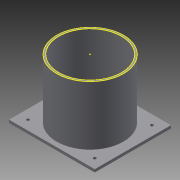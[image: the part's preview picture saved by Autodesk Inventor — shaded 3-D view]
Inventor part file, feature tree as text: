
AUTODESK INVENTOR PART (.ipt)
format: ipt  version: 2013 (Build 170138000, 138)  size: 115,200 bytes
history: native  units: mm
features: sketch x5, extrude x3, other x1, hole x1
ambient origin geometry x8: Origin, YZ Plane, XZ Plane, XY Plane, X Axis, Y Axis, Z Axis, Center Point
feature tree (10):
  other  "ソリッド1"
  extrude  "押し出し1"  Depth=70.0mm
  extrude  "押し出し2"  Depth=66.0mm
  extrude  "押し出し3"  Depth=90.0mm
  sketch  "スケッチ4"
  hole  "穴1"  [1 undecoded]
  sketch  "スケッチ1"
  sketch  "スケッチ2"
  sketch  "スケッチ3"
  sketch  "スケッチ5"
note: 1 required parameter value undecoded (feature->parameter linkage not recoverable at this tier; creation-order binding heuristic only, values carry confidence <= 0.55)
